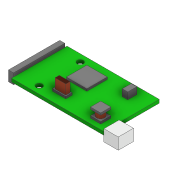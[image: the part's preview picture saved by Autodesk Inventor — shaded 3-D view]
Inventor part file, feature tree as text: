
AUTODESK INVENTOR PART (.ipt)
format: ipt  version: 2022.3 (Build 263350000, 350)  size: 201,216 bytes
history: native  units: mm
features: extrude x9, sketch x9, projected_geometry x3, other x1
ambient origin geometry x8: Origin, YZ Plane, XZ Plane, XY Plane, X Axis, Y Axis, Z Axis, Center Point
bodies: Body1 (feature_tree)
feature tree (22):
  other  "Sólido1"
  extrude  "Extrusión1"  Depth=27.1mm
  extrude  "Extrusión2"  Depth=10.0mm
  extrude  "Extrusión3"  Depth=3.0mm
  extrude  "Extrusión4"  Depth=1.6mm TaperAngle=0.0deg
  extrude  "Extrusión5"  Depth=5.0mm
  extrude  "Extrusión6"  Depth=7.5mm
  extrude  "Extrusión7"  Depth=7.0mm TaperAngle=0.0deg
  extrude  "Extrusión8"  Depth=10.0mm
  extrude  "Extrusión9"  Depth=5.0mm
  sketch  "Boceto1"  dims[d0=45.0mm d1=27.1mm]
  sketch  "Boceto2"  dims[d2=10.0mm d3=10.0mm]
  sketch  "Boceto3"  dims[d4=20.0mm d5=3.0mm]
  sketch  "Boceto4"  dims[d6=3.0mm d7=1.6mm d8=0.0mm]
  sketch  "Boceto5"  dims[d9=25.0mm d10=5.0mm]
  sketch  "Boceto6"  dims[d11=2.5mm d12=0.0mm d13=7.5mm]
  sketch  "Boceto7"  dims[d14=5.6mm d15=7.0mm d16=0.0mm]
  projected_geometry  "Contorno proyectado1"
  projected_geometry  "Contorno proyectado2"
  sketch  "Boceto8"  dims[d17=10.0mm d18=10.0mm]
  projected_geometry  "Contorno proyectado3"
  sketch  "Boceto9"  dims[d19=5.0mm d20=5.0mm d21=1.0mm d22=0.0mm d23=4.7mm d24=0.0mm d25=2.7mm d26=0.0mm d27=1.0mm d28=0.0mm d29=2.3mm d30=0.0mm d31=0.1mm d32=0.0mm]
